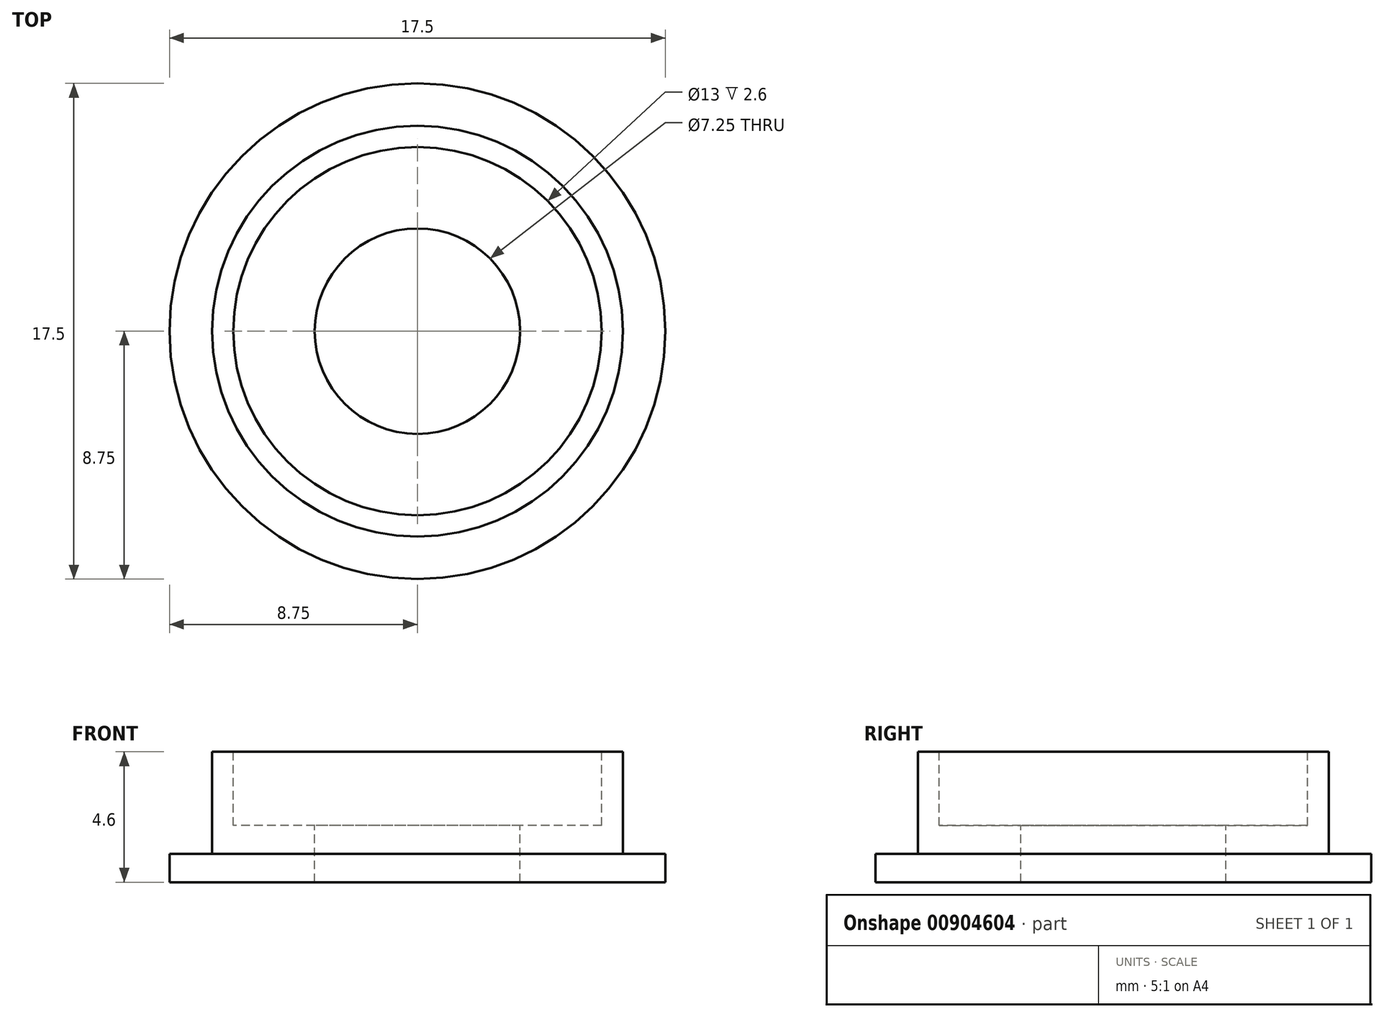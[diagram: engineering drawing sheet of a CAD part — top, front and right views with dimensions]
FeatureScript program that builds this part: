
annotation { "Feature Type Name" : "Feature", "Feature Type Description" : "" }
export const myFeature = defineFeature(function(context is Context, id is Id, definition is map)
    precondition{}
    {
        {
            var Q0;
            Q0=qCreatedBy(makeId("Top.planeOp"),FACE);
            var sketch = newSketch(context, id + "F0", { "sketchPlane" : qUnion([Q0])});
            skCircle(sketch, "E0", {"center": v(0, 0) * mm, "radius": 8.75 * mm});
            skSolve(sketch);
        }
        {
            var Q0;
            Q0=makeQuery(id+"F0.imprint","IMPRINT",FACE,{"disambiguationData":[TD([[makeQuery(id+"F0.imprint","IMPRINT",EDGE,{"derivedFrom":sQuery(id+"F0.wireOp",EDGE,"E0")}),1.0]])]});
            extrude(context, id + "F1", {"entities" : qUnion([Q0]), "depth" : 1 * mm, "offsetDistance" : 25 * mm});
        }
        {
            var Q0;
            Q0=makeQuery(id+"F1.opExtrude","CAP_FACE",FACE,{"disambiguationData":[OSD([sQuery(id+"F0.wireOp",EDGE,"E0")])],"isStart":false});
            var sketch = newSketch(context, id + "F2", { "sketchPlane" : qUnion([Q0])});
            skCircle(sketch, "E1", {"center": v(0, 0) * mm, "radius": 7.25 * mm});
            skSolve(sketch);
        }
        {
            var Q0;
            Q0 = qSketchRegion(id + "F2", true);
            extrude(context, id + "F3", {"entities" : qUnion([Q0]), "operationType" : NewBodyOperationType.ADD, "depth" : 3.6 * mm, "offsetDistance" : 25 * mm});
        }
        {
            var Q0;
            Q0=makeQuery(id+"F3.opExtrude","CAP_FACE",FACE,{"disambiguationData":[OSD([sQuery(id+"F2.wireOp",EDGE,"E1")])],"isStart":false});
            var sketch = newSketch(context, id + "F4", { "sketchPlane" : qUnion([Q0])});
            skCircle(sketch, "E2", {"center": v(0, 0) * mm, "radius": 6.5 * mm});
            skSolve(sketch);
        }
        {
            var Q0;
            Q0=makeQuery(id+"F4.imprint","IMPRINT",FACE,{"disambiguationData":[TD([[makeQuery(id+"F4.imprint","IMPRINT",EDGE,{"derivedFrom":sQuery(id+"F4.wireOp",EDGE,"E2")}),1.0]])]});
            extrude(context, id + "F5", {"entities" : qUnion([Q0]), "operationType" : NewBodyOperationType.REMOVE, "oppositeDirection" : true, "depth" : 2.6 * mm, "offsetDistance" : 25 * mm});
        }
        {
            var Q0;
            Q0=makeQuery(id+"F5.boolean.opBoolean","COPY",FACE,{"derivedFrom":makeQuery(id+"F5.opExtrude","CAP_FACE",FACE,{"disambiguationData":[OSD([sQuery(id+"F4.wireOp",EDGE,"E2")])],"isStart":false})});
            var sketch = newSketch(context, id + "F6", { "sketchPlane" : qUnion([Q0])});
            skCircle(sketch, "E3", {"center": v(0, 0) * mm, "radius": 3.63 * mm});
            skSolve(sketch);
        }
        {
            var Q0;
            Q0=makeQuery(id+"F6.imprint","IMPRINT",FACE,{"disambiguationData":[TD([[makeQuery(id+"F6.imprint","IMPRINT",EDGE,{"derivedFrom":sQuery(id+"F6.wireOp",EDGE,"E3")}),1.0]])]});
            extrude(context, id + "F7", {"entities" : qUnion([Q0]), "operationType" : NewBodyOperationType.REMOVE, "endBound" : BoundingType.THROUGH_ALL, "oppositeDirection" : true, "depth" : 25 * mm, "offsetDistance" : 25 * mm});
        }
    });
